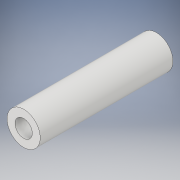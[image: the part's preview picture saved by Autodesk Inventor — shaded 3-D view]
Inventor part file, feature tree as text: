
AUTODESK INVENTOR PART (.ipt)
format: ipt  version: 2017 (Build 210142000, 142)  size: 96,256 bytes
history: native  units: in
note: dims shown in document units (in); Inventor stores cm internally (conversion verified against a paired STEP export)
features: extrude x1, sketch x1
ambient origin geometry x8: Origin, YZ Plane, XZ Plane, XY Plane, X Axis, Y Axis, Z Axis, Center Point
bodies: Solid1 (feature_tree)
feature tree (2):
  extrude  "Extrusion1"  Depth=2.0in
  sketch  "Sketch1"  dims[d0=0.26in d1=0.5in d2=2.0in d3=0.0in]
